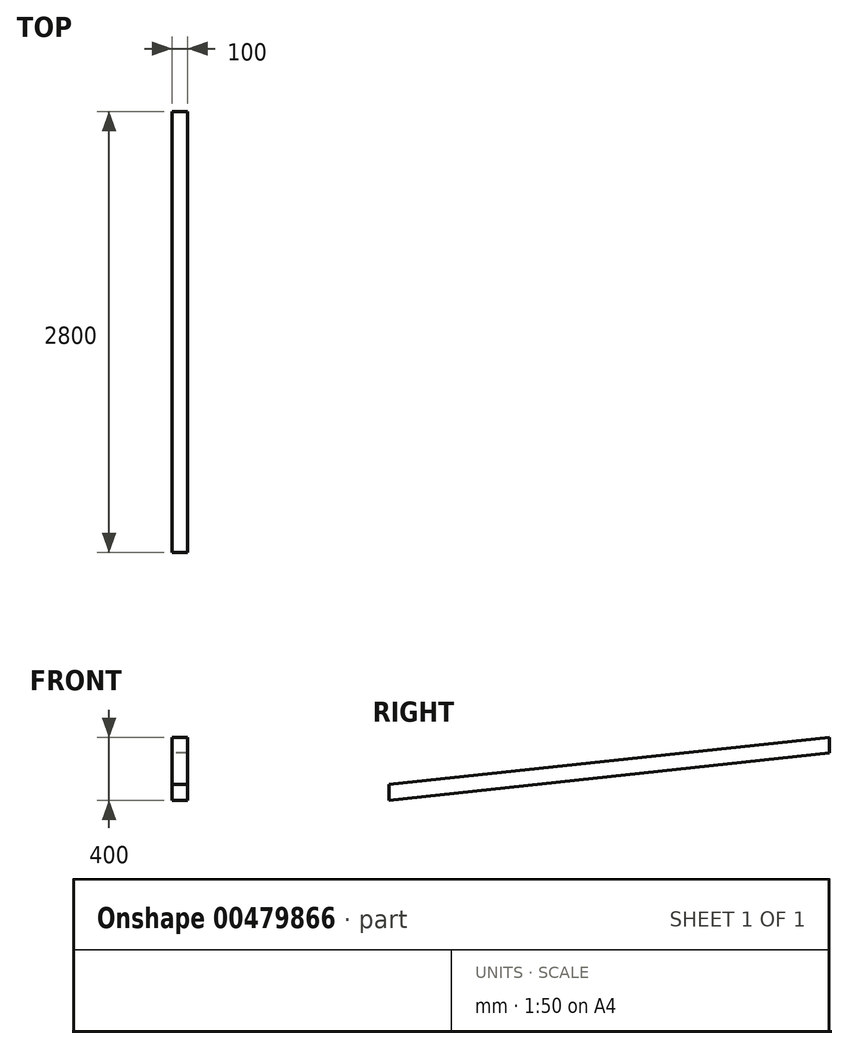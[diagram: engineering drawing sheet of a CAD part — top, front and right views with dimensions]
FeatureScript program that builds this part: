
annotation { "Feature Type Name" : "Feature", "Feature Type Description" : "" }
export const myFeature = defineFeature(function(context is Context, id is Id, definition is map)
    precondition{}
    {
        {
            var Q0;
            Q0=qCreatedBy(makeId("Right.planeOp"),FACE);
            var sketch = newSketch(context, id + "F0", { "sketchPlane" : qUnion([Q0])});
            skLineSegment(sketch, "E0", {"start": v(0, 0) * mm, "end": v(0, -100) * mm});
            skLineSegment(sketch, "E1", {"start": v(0, -100) * mm, "end": v(-2800, -400) * mm});
            skLineSegment(sketch, "E2", {"start": v(-2800, -400) * mm, "end": v(-2800, -300) * mm});
            skLineSegment(sketch, "E3", {"start": v(-2800, -300) * mm, "end": v(0, 0) * mm});
            skSolve(sketch);
        }
        {
            var Q0;
            Q0=makeQuery(id+"F0.imprint","IMPRINT",FACE,{"disambiguationData":[TD([[makeQuery(id+"F0.imprint","IMPRINT",EDGE,{"derivedFrom":sQuery(id+"F0.wireOp",EDGE,"E0")}),-1.0]])]});
            extrude(context, id + "F1", {"entities" : qUnion([Q0]), "depth" : 100 * mm});
        }
    });
